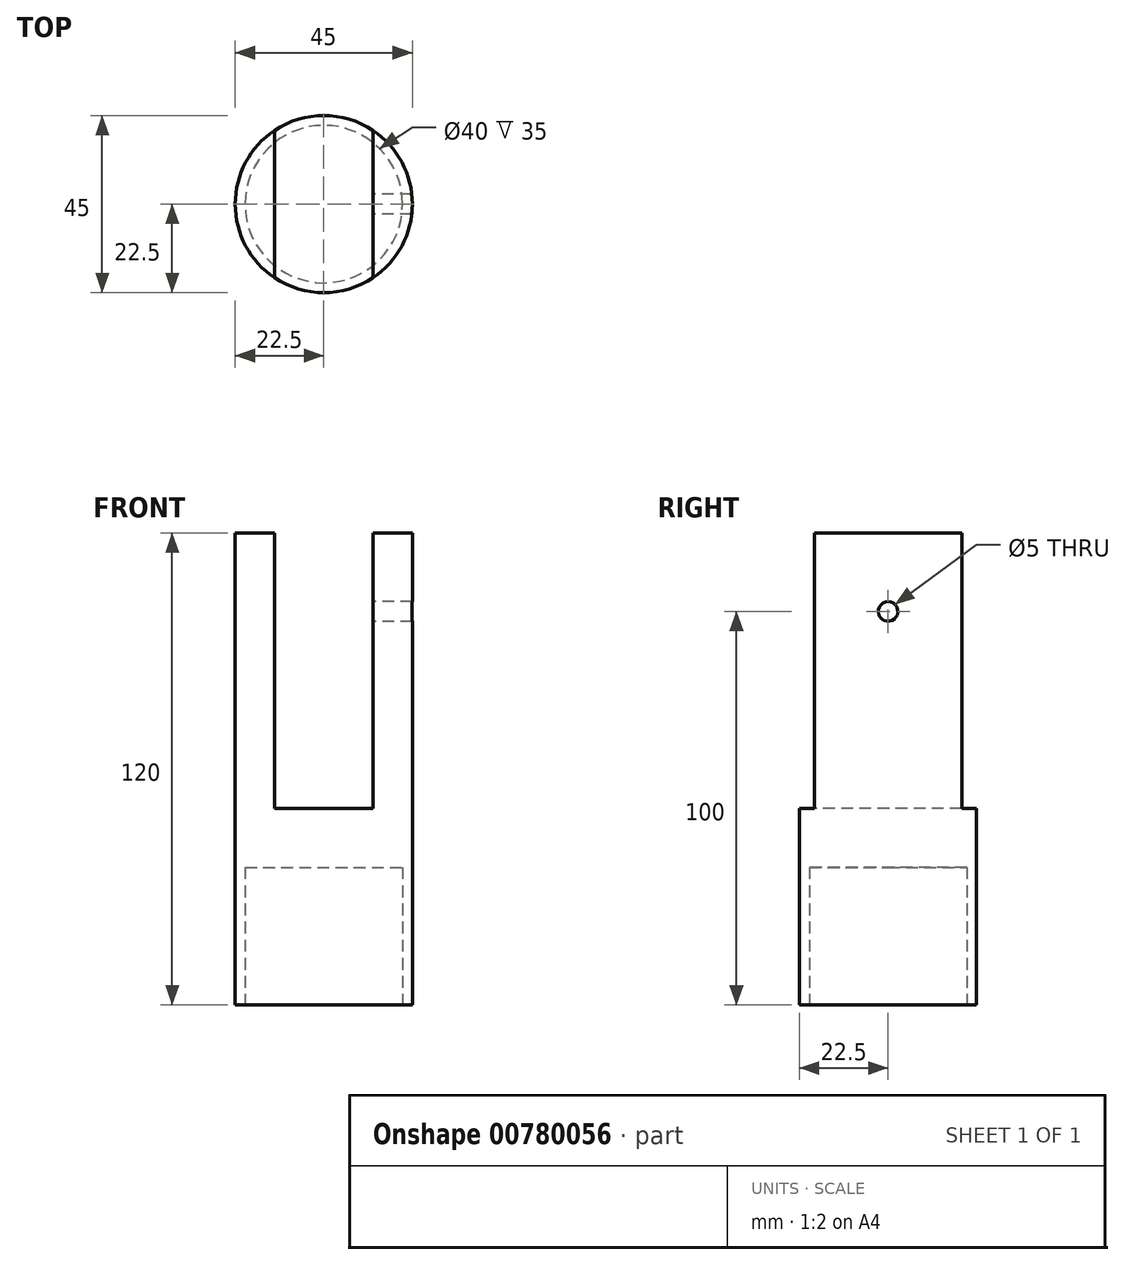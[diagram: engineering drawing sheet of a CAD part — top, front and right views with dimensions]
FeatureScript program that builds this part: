
annotation { "Feature Type Name" : "Feature", "Feature Type Description" : "" }
export const myFeature = defineFeature(function(context is Context, id is Id, definition is map)
    precondition{}
    {
        {
            var Q0;
            Q0=qCreatedBy(makeId("Top.planeOp"),FACE);
            var sketch = newSketch(context, id + "F0", { "sketchPlane" : qUnion([Q0])});
            skCircle(sketch, "E0", {"center": v(0, 0) * mm, "radius": 22.5 * mm});
            skSolve(sketch);
        }
        {
            var Q0;
            Q0=makeQuery(id+"F0.imprint","IMPRINT",FACE,{"disambiguationData":[TD([[makeQuery(id+"F0.imprint","IMPRINT",EDGE,{"derivedFrom":sQuery(id+"F0.wireOp",EDGE,"E0")}),1.0]])]});
            extrude(context, id + "F1", {"entities" : qUnion([Q0]), "depth" : 120 * mm, "offsetDistance" : 25 * mm});
        }
        {
            var Q0;
            Q0=makeQuery(id+"F1.opExtrude","CAP_FACE",FACE,{"disambiguationData":[OSD([sQuery(id+"F0.wireOp",EDGE,"E0")])],"isStart":false});
            var sketch = newSketch(context, id + "F2", { "sketchPlane" : qUnion([Q0])});
            skLineSegment(sketch, "E1", {"start": v(-12.5, 18.7) * mm, "end": v(-12.5, -18.7) * mm});
            skLineSegment(sketch, "E2", {"start": v(12.5, -18.7) * mm, "end": v(12.5, 18.7) * mm});
            skSolve(sketch);
        }
        {
            var Q0;
            {var subQ0=sQuery(id+"F2.wireOp",EDGE,"E1");Q0=makeQuery(id+"F2.imprint","IMPRINT",FACE,{"disambiguationData":[TD([[makeQuery(id+"F2.imprint","IMPRINT",EDGE,{"derivedFrom":subQ0}),1.0]])]});}
            extrude(context, id + "F3", {"entities" : qUnion([Q0]), "operationType" : NewBodyOperationType.REMOVE, "oppositeDirection" : true, "depth" : 70 * mm, "offsetDistance" : 25 * mm});
        }
        {
            var Q0;
            Q0=makeQuery(id+"F1.opExtrude","CAP_FACE",FACE,{"disambiguationData":[OSD([sQuery(id+"F0.wireOp",EDGE,"E0")])],"isStart":true});
            var sketch = newSketch(context, id + "F4", { "sketchPlane" : qUnion([Q0])});
            skCircle(sketch, "E3", {"center": v(0, 0) * mm, "radius": 20 * mm});
            skSolve(sketch);
        }
        {
            var Q0;
            Q0=makeQuery(id+"F4.imprint","IMPRINT",FACE,{"disambiguationData":[TD([[makeQuery(id+"F4.imprint","IMPRINT",EDGE,{"derivedFrom":sQuery(id+"F4.wireOp",EDGE,"E3")}),1.0]])]});
            extrude(context, id + "F5", {"entities" : qUnion([Q0]), "operationType" : NewBodyOperationType.REMOVE, "oppositeDirection" : true, "depth" : 35 * mm, "offsetDistance" : 25 * mm});
        }
        {
            var Q0;
            Q0=makeQuery(id+"F3.boolean.opBoolean","COPY",FACE,{"derivedFrom":makeQuery(id+"F3.opExtrude","SWEPT_FACE",FACE,{"disambiguationData":[OSD([sQuery(id+"F2.wireOp",EDGE,"E2")])]})});
            var sketch = newSketch(context, id + "F6", { "sketchPlane" : qUnion([Q0])});
            skPoint(sketch, "E4", {"position": v(0, 100) * mm});
            skSolve(sketch);
        }
        {
            var Q0;
            Q0=sQuery(id+"F6.wireOp",VERTEX,"E4");
            var Q1;
            Q1=makeQuery(id+"F1.opExtrude","SWEPT_BODY",BODY,{"disambiguationData":[OSD([sQuery(id+"F0.wireOp",EDGE,"E0")])]});
            hole(context, id + "F7", {"style" : HoleStyle.SIMPLE, "endStyle" : HoleEndStyle.BLIND, "holeDiameter" : 5 * mm, "majorDiameter" : 5 * mm, "holeDepth" : 12 * mm, "isTappedThrough" : true, "tappedDepth" : 12 * mm, "tapClearance" : 3, "locations" : qUnion([Q0]), "scope" : qUnion([Q1])});
        }
    });
